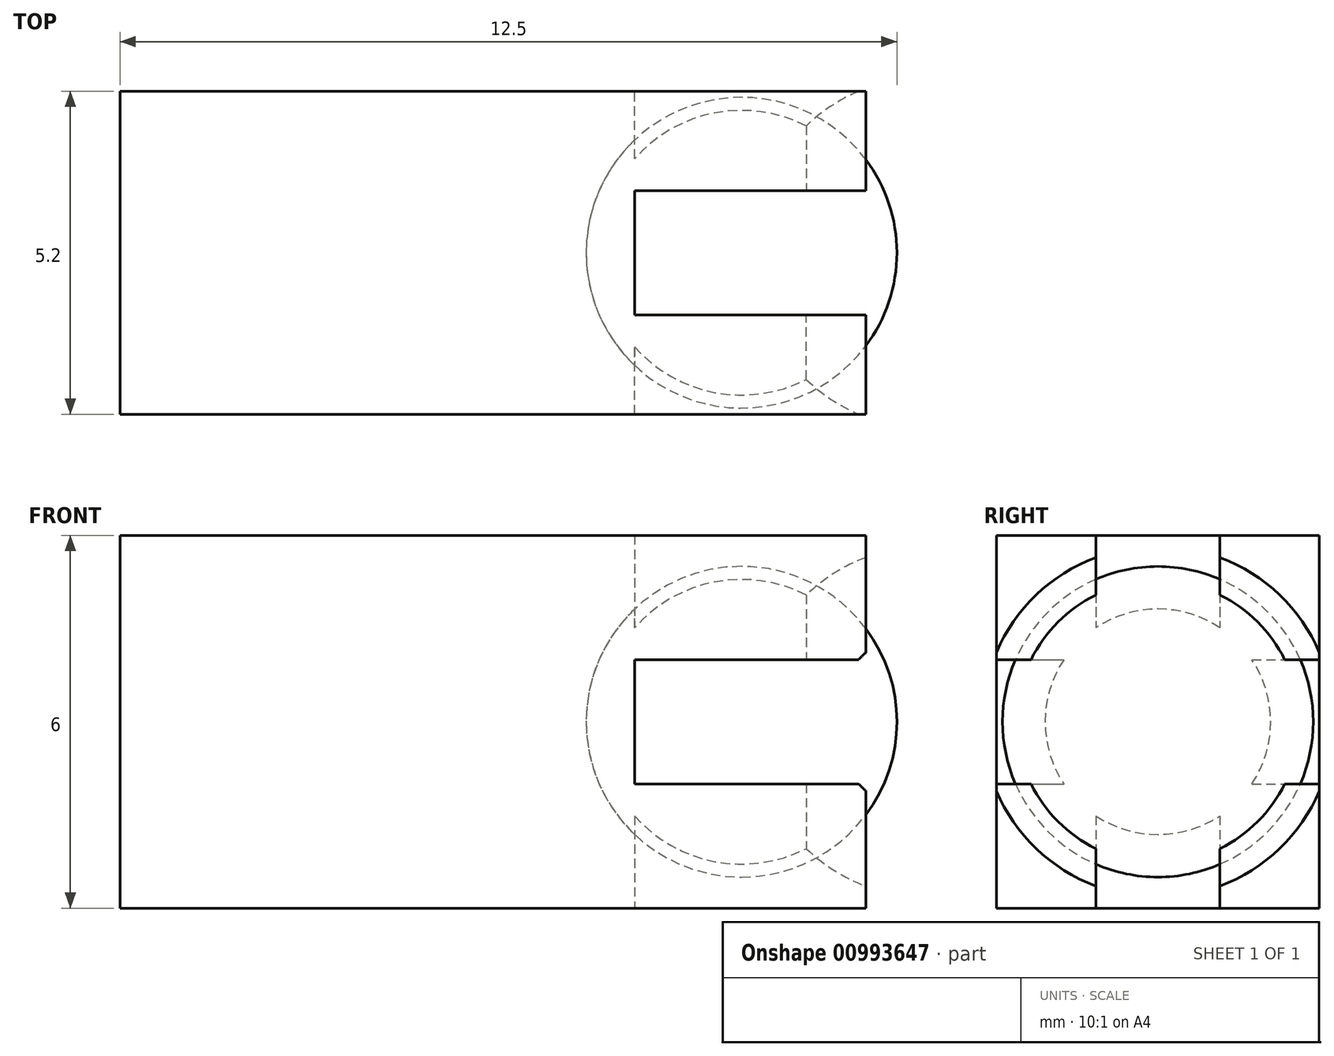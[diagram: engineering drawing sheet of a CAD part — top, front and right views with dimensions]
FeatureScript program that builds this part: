
annotation { "Feature Type Name" : "Feature", "Feature Type Description" : "" }
export const myFeature = defineFeature(function(context is Context, id is Id, definition is map)
    precondition{}
    {
        {
            var Q0;
            Q0=qCreatedBy(makeId("Front.planeOp"),FACE);
            var sketch = newSketch(context, id + "F0", { "sketchPlane" : qUnion([Q0])});
            skArc(sketch, "E0", {"start": v(0, 2.5) * mm, "mid": v(-2.5, 0) * mm, "end": v(0, -2.5) * mm});
            skLineSegment(sketch, "E1", {"start": v(0, 2.5) * mm, "end": v(0, -2.5) * mm});
            skLineSegment(sketch, "E2", {"start": v(-6.75, 0) * mm, "end": v(7.5, 0) * mm, "construction": true});
            skSolve(sketch);
        }
        {
            var Q0;
            Q0 = qSketchRegion(id + "F0", true);
            var Q1;
            Q1=sQuery(id+"F0.wireOp",EDGE,"E1");
            revolve(context, id + "F1", {"surfaceOperationType" : NewSurfaceOperationType.NEW, "entities" : qUnion([Q0]), "axis" : qUnion([Q1]), "revolveType" : RevolveType.FULL});
        }
        {
            var Q0;
            Q0=qCreatedBy(makeId("Top.planeOp"),FACE);
            var sketch = newSketch(context, id + "F2", { "sketchPlane" : qUnion([Q0])});
            skPoint(sketch, "E3.middle", {"position": v(0, 0) * mm});
            skLineSegment(sketch, "E4", {"start": v(2, 0) * mm, "end": v(-10, 0) * mm, "construction": true});
            skLineSegment(sketch, "E5", {"start": v(2, 2.6) * mm, "end": v(-10, 2.6) * mm});
            skLineSegment(sketch, "E6", {"start": v(-10, 2.6) * mm, "end": v(-10, 0) * mm});
            skLineSegment(sketch, "E7", {"start": v(2, 2.6) * mm, "end": v(2, 0) * mm});
            skLineSegment(sketch, "E8.MirrorCS", {"start": v(-10, -2.6) * mm, "end": v(-10, 0) * mm});
            skLineSegment(sketch, "E9.MirrorCS", {"start": v(2, -2.6) * mm, "end": v(2, 0) * mm});
            skLineSegment(sketch, "E10.MirrorCS", {"start": v(2, -2.6) * mm, "end": v(-10, -2.6) * mm});
            skSolve(sketch);
        }
        {
            var Q0;
            Q0=makeQuery(id+"F2.imprint","IMPRINT",FACE,{"disambiguationData":[TD([[makeQuery(id+"F2.imprint","IMPRINT",EDGE,{"derivedFrom":sQuery(id+"F2.wireOp",EDGE,"E5")}),1.0]])]});
            extrude(context, id + "F3", {"entities" : qUnion([Q0]), "endBound" : BoundingType.SYMMETRIC, "depth" : 6 * mm, "offsetDistance" : 25 * mm});
        }
        {
            var Q0;
            Q0=makeQuery(id+"F1.opRevolve","SWEPT_BODY",BODY,{"disambiguationData":[OSD([sQuery(id+"F0.wireOp",EDGE,"E0"),sQuery(id+"F0.wireOp",EDGE,"E1")])]});
            var Q1;
            Q1=makeQuery(id+"F3.opExtrude","SWEPT_BODY",BODY,{"disambiguationData":[OSD([sQuery(id+"F2.wireOp",EDGE,"E5"),sQuery(id+"F2.wireOp",EDGE,"E6"),sQuery(id+"F2.wireOp",EDGE,"E7"),sQuery(id+"F2.wireOp",EDGE,"E8.MirrorCS"),sQuery(id+"F2.wireOp",EDGE,"E9.MirrorCS"),sQuery(id+"F2.wireOp",EDGE,"E10.MirrorCS")])]});
            booleanBodies(context, id + "F4", {"operationType" : BooleanOperationType.SUBTRACTION, "tools" : qUnion([Q0]), "targets" : qUnion([Q1]), "keepTools" : true});
        }
        {
            var Q0;
            Q0=qCreatedBy(makeId("Top.planeOp"),FACE);
            var sketch = newSketch(context, id + "F5", { "sketchPlane" : qUnion([Q0])});
            skLineSegment(sketch, "E11.bottom", {"start": v(2.5, -1) * mm, "end": v(-1.72, -1) * mm});
            skLineSegment(sketch, "E11.top", {"start": v(2.5, 1) * mm, "end": v(-1.72, 1) * mm});
            skLineSegment(sketch, "E11.left", {"start": v(2.5, -1) * mm, "end": v(2.5, 1) * mm});
            skPoint(sketch, "E11.middle", {"position": v(0, 0) * mm});
            skLineSegment(sketch, "E12", {"start": v(-1.72, 2.98) * mm, "end": v(-1.72, -2.83) * mm, "construction": true});
            skLineSegment(sketch, "E13", {"start": v(-1.72, 1) * mm, "end": v(-1.72, -1) * mm});
            skSolve(sketch);
        }
        {
            var Q0;
            Q0=makeQuery(id+"F5.imprint","IMPRINT",FACE,{"disambiguationData":[TD([[makeQuery(id+"F5.imprint","IMPRINT",EDGE,{"derivedFrom":sQuery(id+"F5.wireOp",EDGE,"E11.bottom")}),-1.0]])]});
            extrude(context, id + "F6", {"entities" : qUnion([Q0]), "endBound" : BoundingType.SYMMETRIC, "depth" : 8 * mm, "offsetDistance" : 25 * mm});
        }
        {
            var Q0;
            Q0=makeQuery(id+"F6.opExtrude","SWEPT_BODY",BODY,{"disambiguationData":[OSD([sQuery(id+"F5.wireOp",EDGE,"E11.bottom"),sQuery(id+"F5.wireOp",EDGE,"E11.top"),sQuery(id+"F5.wireOp",EDGE,"E11.left"),sQuery(id+"F5.wireOp",EDGE,"E11.right")])]});
            var Q1;
            Q1=sQuery(id+"F0.wireOp",EDGE,"E2");
            transform(context, id + "F7", {"entities" : qUnion([Q0]), "transformType" : TransformType.ROTATION, "transformAxis" : qUnion([Q1]), "angle" : 90 * degree, "makeCopy" : true});
        }
        {
            var Q0;
            Q0=makeQuery(id+"F7.opPattern","COPY",BODY,{"derivedFrom":makeQuery(id+"F6.opExtrude","SWEPT_BODY",BODY,{"disambiguationData":[OSD([sQuery(id+"F5.wireOp",EDGE,"E11.bottom"),sQuery(id+"F5.wireOp",EDGE,"E11.top"),sQuery(id+"F5.wireOp",EDGE,"E11.left"),sQuery(id+"F5.wireOp",EDGE,"E11.right")])]}),"instanceName":"1"});
            var Q1;
            Q1=makeQuery(id+"F3.opExtrude","SWEPT_BODY",BODY,{"disambiguationData":[OSD([sQuery(id+"F2.wireOp",EDGE,"E5"),sQuery(id+"F2.wireOp",EDGE,"E6"),sQuery(id+"F2.wireOp",EDGE,"E7"),sQuery(id+"F2.wireOp",EDGE,"E8.MirrorCS"),sQuery(id+"F2.wireOp",EDGE,"E9.MirrorCS"),sQuery(id+"F2.wireOp",EDGE,"E10.MirrorCS")])]});
            booleanBodies(context, id + "F8", {"operationType" : BooleanOperationType.SUBTRACTION, "tools" : qUnion([Q0]), "targets" : qUnion([Q1])});
        }
        {
            var Q0;
            Q0=makeQuery(id+"F6.opExtrude","SWEPT_BODY",BODY,{"disambiguationData":[OSD([sQuery(id+"F5.wireOp",EDGE,"E11.bottom"),sQuery(id+"F5.wireOp",EDGE,"E11.top"),sQuery(id+"F5.wireOp",EDGE,"E11.left"),sQuery(id+"F5.wireOp",EDGE,"E11.right")])]});
            var Q1;
            Q1=makeQuery(id+"F3.opExtrude","SWEPT_BODY",BODY,{"disambiguationData":[OSD([sQuery(id+"F2.wireOp",EDGE,"E5"),sQuery(id+"F2.wireOp",EDGE,"E6"),sQuery(id+"F2.wireOp",EDGE,"E7"),sQuery(id+"F2.wireOp",EDGE,"E8.MirrorCS"),sQuery(id+"F2.wireOp",EDGE,"E9.MirrorCS"),sQuery(id+"F2.wireOp",EDGE,"E10.MirrorCS")])]});
            booleanBodies(context, id + "F9", {"operationType" : BooleanOperationType.SUBTRACTION, "tools" : qUnion([Q0]), "targets" : qUnion([Q1])});
        }
        {
            var Q0;
            Q0=makeQuery(id+"F1.opRevolve","SWEPT_BODY",BODY,{"disambiguationData":[OSD([sQuery(id+"F0.wireOp",EDGE,"E0"),sQuery(id+"F0.wireOp",EDGE,"E1")])]});
            var Q1;
            Q1=qCreatedBy(makeId("Origin.pointOp"),VERTEX);
            transform(context, id + "F10", {"entities" : qUnion([Q0]), "transformType" : TransformType.SCALE_UNIFORMLY, "scale" : 1.2, "scalePoint" : qUnion([Q1]), "makeCopy" : true});
        }
        {
            var Q0;
            Q0=makeQuery(id+"F10.opPattern","COPY",BODY,{"derivedFrom":makeQuery(id+"F1.opRevolve","SWEPT_BODY",BODY,{"disambiguationData":[OSD([sQuery(id+"F0.wireOp",EDGE,"E0"),sQuery(id+"F0.wireOp",EDGE,"E1")])]}),"instanceName":"1"});
            transform(context, id + "F11", {"entities" : qUnion([Q0]), "transformType" : TransformType.TRANSLATION_3D, "dx" : 3 * mm, "dy" : 0 * mm, "dz" : 0 * mm, "makeCopy" : false});
        }
        {
            var Q0;
            Q0=makeQuery(id+"F10.opPattern","COPY",BODY,{"derivedFrom":makeQuery(id+"F1.opRevolve","SWEPT_BODY",BODY,{"disambiguationData":[OSD([sQuery(id+"F0.wireOp",EDGE,"E0"),sQuery(id+"F0.wireOp",EDGE,"E1")])]}),"instanceName":"1"});
            var Q1;
            Q1=makeQuery(id+"F3.opExtrude","SWEPT_BODY",BODY,{"disambiguationData":[OSD([sQuery(id+"F2.wireOp",EDGE,"E5"),sQuery(id+"F2.wireOp",EDGE,"E6"),sQuery(id+"F2.wireOp",EDGE,"E7"),sQuery(id+"F2.wireOp",EDGE,"E8.MirrorCS"),sQuery(id+"F2.wireOp",EDGE,"E9.MirrorCS"),sQuery(id+"F2.wireOp",EDGE,"E10.MirrorCS")])]});
            booleanBodies(context, id + "F12", {"operationType" : BooleanOperationType.SUBTRACTION, "tools" : qUnion([Q0]), "targets" : qUnion([Q1])});
        }
    });
